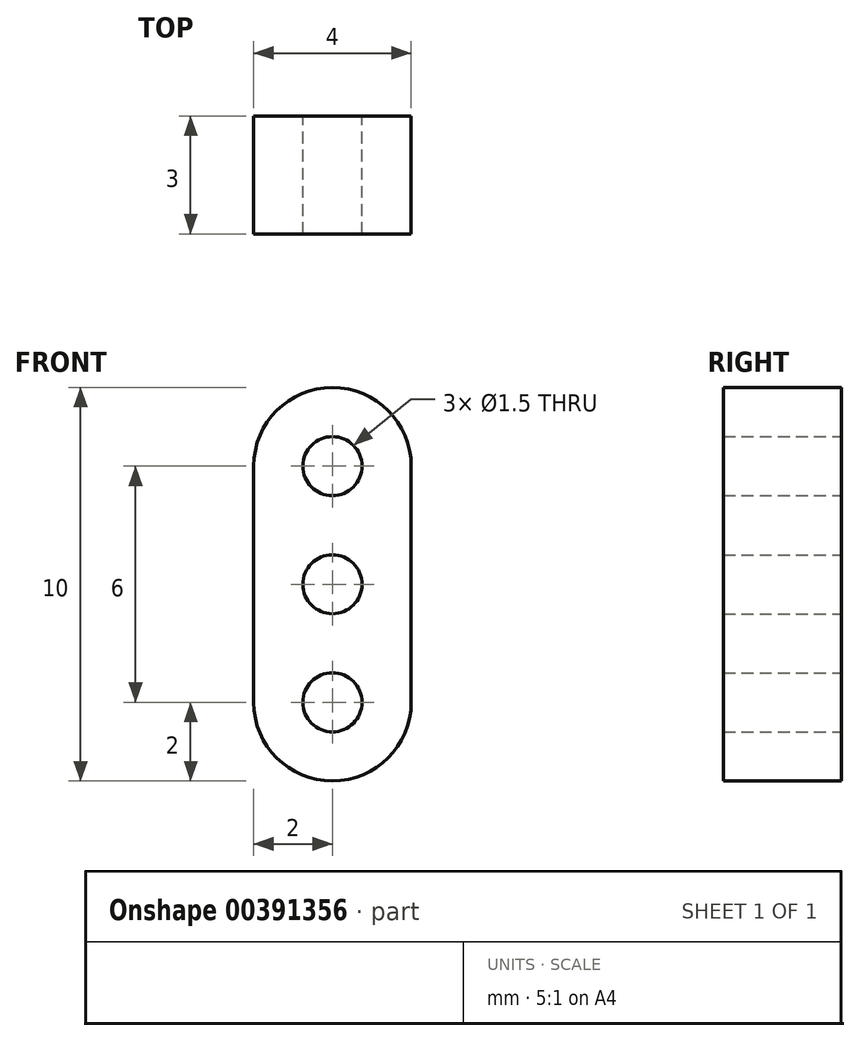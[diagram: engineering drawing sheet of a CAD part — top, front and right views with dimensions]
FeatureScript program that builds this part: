
annotation { "Feature Type Name" : "Feature", "Feature Type Description" : "" }
export const myFeature = defineFeature(function(context is Context, id is Id, definition is map)
    precondition{}
    {
        {
            var Q0;
            Q0=qCreatedBy(makeId("Front.planeOp"),FACE);
            var sketch = newSketch(context, id + "F0", { "sketchPlane" : qUnion([Q0])});
            skCircle(sketch, "E0", {"center": v(0, 3) * mm, "radius": 0.75 * mm});
            skCircle(sketch, "E1", {"center": v(0, -3) * mm, "radius": 0.75 * mm});
            skCircle(sketch, "E2", {"center": v(0, 0) * mm, "radius": 0.75 * mm});
            skLineSegment(sketch, "E3", {"start": v(-2, 3) * mm, "end": v(-2, -3) * mm});
            skLineSegment(sketch, "E4", {"start": v(2, 3) * mm, "end": v(2, -3) * mm});
            skArc(sketch, "E5", {"start": v(2, 3) * mm, "mid": v(0, 5) * mm, "end": v(-2, 3) * mm});
            skArc(sketch, "E6", {"start": v(-2, -3) * mm, "mid": v(0, -5) * mm, "end": v(2, -3) * mm});
            skSolve(sketch);
        }
        {
            var Q0;
            Q0 = qSketchRegion(id + "F0", true);
            extrude(context, id + "F1", {"entities" : qUnion([Q0]), "depth" : 3 * mm});
        }
    });
